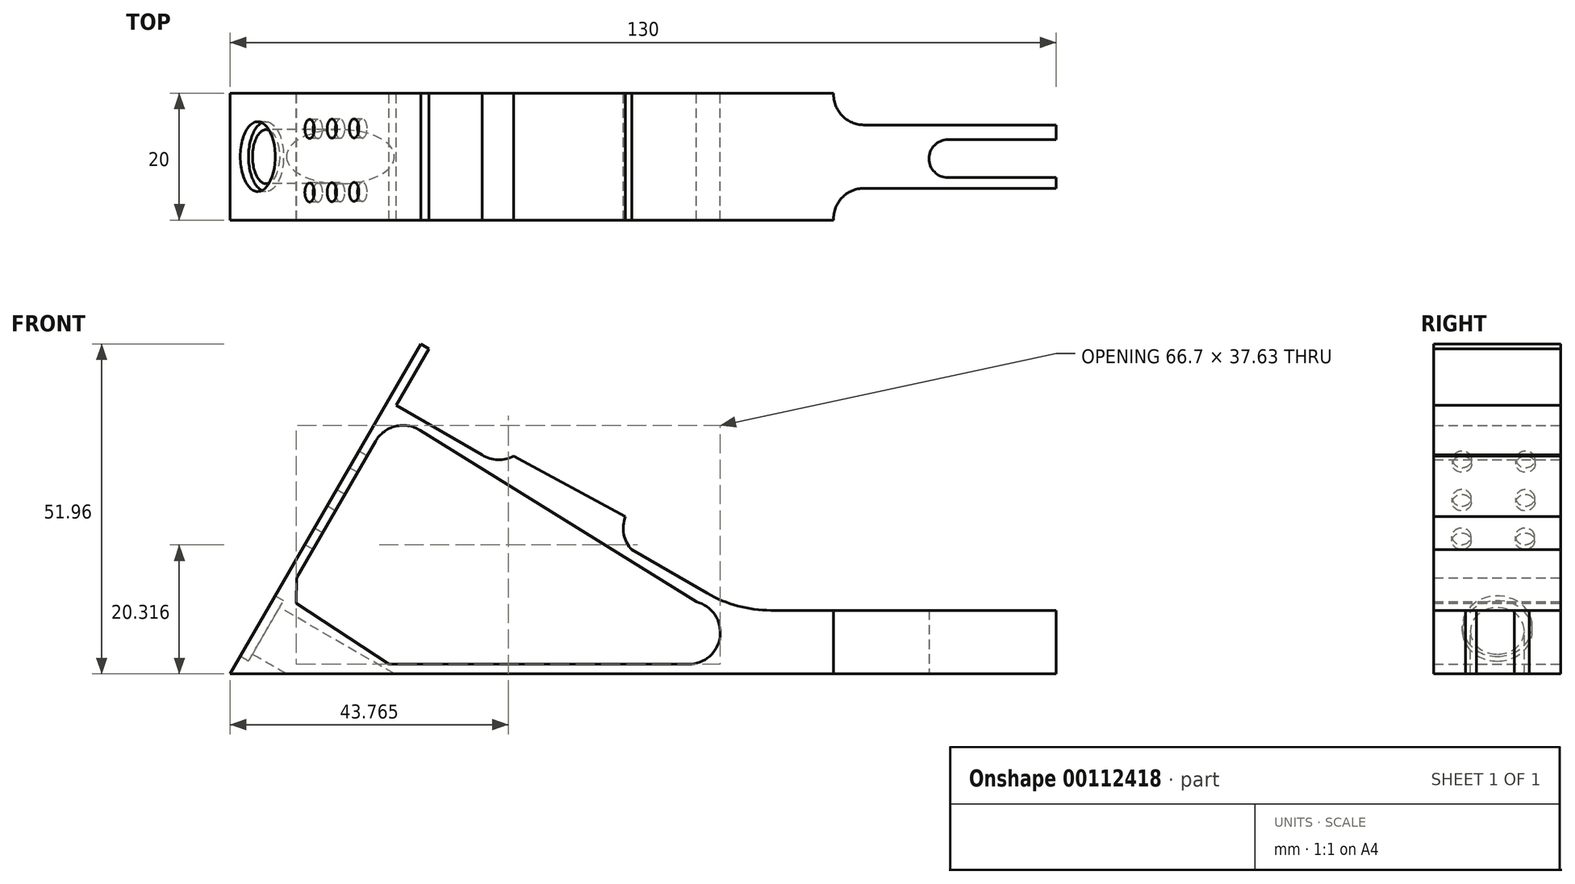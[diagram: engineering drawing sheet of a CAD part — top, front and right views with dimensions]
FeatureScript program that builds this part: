
annotation { "Feature Type Name" : "Feature", "Feature Type Description" : "" }
export const myFeature = defineFeature(function(context is Context, id is Id, definition is map)
    precondition{}
    {
        {
            var Q0;
            Q0=qCreatedBy(makeId("Front.planeOp"),FACE);
            var sketch = newSketch(context, id + "F0", { "sketchPlane" : qUnion([Q0])});
            skLineSegment(sketch, "E0", {"start": v(0, 0) * mm, "end": v(130, 0) * mm});
            skLineSegment(sketch, "E1", {"start": v(30, 51.96) * mm, "end": v(0, 0) * mm});
            skLineSegment(sketch, "E2", {"start": v(130, 0) * mm, "end": v(130, 10) * mm});
            skLineSegment(sketch, "E3", {"start": v(130, 10) * mm, "end": v(85.1, 10) * mm});
            skLineSegment(sketch, "E4", {"start": v(75.1, 12.68) * mm, "end": v(63.23, 19.53) * mm});
            skLineSegment(sketch, "E5", {"start": v(62.2, 24.74) * mm, "end": v(44.64, 34.31) * mm});
            skLineSegment(sketch, "E6", {"start": v(39.66, 34.46) * mm, "end": v(26.13, 42.26) * mm});
            skLineSegment(sketch, "E7", {"start": v(26.13, 42.26) * mm, "end": v(31.3, 51.21) * mm});
            skLineSegment(sketch, "E8", {"start": v(31.3, 51.21) * mm, "end": v(30, 51.96) * mm});
            skArc(sketch, "E9.filletArc", {"start": v(75.1, 12.68) * mm, "mid": v(79.93, 10.68) * mm, "end": v(85.1, 10) * mm});
            skArc(sketch, "E10", {"start": v(44.64, 34.31) * mm, "mid": v(42.13, 33.72) * mm, "end": v(39.66, 34.46) * mm});
            skArc(sketch, "E11", {"start": v(62.2, 24.74) * mm, "mid": v(61.97, 22) * mm, "end": v(63.23, 19.53) * mm});
            skLineSegment(sketch, "E12", {"start": v(10.46, 15.12) * mm, "end": v(22.88, 36.64) * mm});
            skLineSegment(sketch, "E13", {"start": v(29.85, 38.39) * mm, "end": v(73.39, 11.35) * mm});
            skPoint(sketch, "E14.visualSharp", {"position": v(25.47, 41.1) * mm});
            skArc(sketch, "E14.filletArc", {"start": v(29.85, 38.39) * mm, "mid": v(26, 38.99) * mm, "end": v(22.88, 36.64) * mm});
            skLineSegment(sketch, "E15", {"start": v(10.46, 15.12) * mm, "end": v(10.42, 11.1) * mm});
            skLineSegment(sketch, "E16", {"start": v(10.42, 11.1) * mm, "end": v(25, 1.5) * mm});
            skLineSegment(sketch, "E17", {"start": v(25, 1.5) * mm, "end": v(72.15, 1.5) * mm});
            skArc(sketch, "E18", {"start": v(72.15, 1.5) * mm, "mid": v(77.11, 5.88) * mm, "end": v(73.39, 11.35) * mm});
            skSolve(sketch);
        }
        {
            var Q0;
            Q0 = qSketchRegion(id + "F0", true);
            extrude(context, id + "F1", {"entities" : qUnion([Q0]), "depth" : 20 * mm});
        }
        {
            var Q0;
            Q0=makeQuery(id+"F1.opExtrude","SWEPT_EDGE",EDGE,{"disambiguationData":[OSD([sQuery(id+"F0.wireOp",EDGE,"E2"),sQuery(id+"F0.wireOp",EDGE,"E3")])]});
            cPlane(context, id + "F2", {"entities" : qUnion([Q0]), "cplaneType" : CPlaneType.LINE_ANGLE, "offset" : 25 * mm, "angle" : 45 * degree, "width" : 150 * mm, "height" : 150 * mm});
        }
        {
            var Q0;
            Q0=qCreatedBy(id+"F2.planeOp",FACE);
            var sketch = newSketch(context, id + "F3", { "sketchPlane" : qUnion([Q0])});
            skLineSegment(sketch, "E19", {"start": v(13.04, -9.66) * mm, "end": v(21.04, -9.66) * mm});
            skArc(sketch, "E20.0.startCap", {"start": v(13.04, -13.66) * mm, "mid": v(9.04, -9.66) * mm, "end": v(13.04, -5.66) * mm});
            skArc(sketch, "E20.0.endCap", {"start": v(21.04, -5.66) * mm, "mid": v(25.04, -9.66) * mm, "end": v(21.04, -13.66) * mm});
            skLineSegment(sketch, "E20.0.left", {"start": v(13.04, -5.66) * mm, "end": v(21.04, -5.66) * mm});
            skLineSegment(sketch, "E20.0.right", {"start": v(13.04, -13.66) * mm, "end": v(21.04, -13.66) * mm});
            skSolve(sketch);
        }
        {
            var Q0;
            Q0 = qSketchRegion(id + "F3", true);
            extrude(context, id + "F4", {"entities" : qUnion([Q0]), "operationType" : NewBodyOperationType.REMOVE, "oppositeDirection" : true, "depth" : 50 * mm});
        }
        {
            var Q0;
            Q0=qCreatedBy(makeId("Top.planeOp"),FACE);
            var sketch = newSketch(context, id + "F5", { "sketchPlane" : qUnion([Q0])});
            skLineSegment(sketch, "E21", {"start": v(95, 0) * mm, "end": v(130, 0) * mm});
            skLineSegment(sketch, "E22", {"start": v(95, -20) * mm, "end": v(130, -20) * mm});
            skLineSegment(sketch, "E23", {"start": v(130, -20) * mm, "end": v(130, -15) * mm});
            skLineSegment(sketch, "E24", {"start": v(130, -5) * mm, "end": v(99.74, -5) * mm});
            skLineSegment(sketch, "E25", {"start": v(130, -15) * mm, "end": v(99.74, -15) * mm});
            skLineSegment(sketch, "E26", {"start": v(130, -13.3) * mm, "end": v(113, -13.3) * mm});
            skLineSegment(sketch, "E27", {"start": v(130, -7.3) * mm, "end": v(113, -7.3) * mm});
            skArc(sketch, "E28", {"start": v(113, -7.3) * mm, "mid": v(110, -10.3) * mm, "end": v(113, -13.3) * mm});
            skLineSegment(sketch, "E29", {"start": v(113, -13.3) * mm, "end": v(113, -7.3) * mm});
            skLineSegment(sketch, "E30", {"start": v(130, 0) * mm, "end": v(130, -5) * mm});
            skArc(sketch, "E31", {"start": v(99.74, -15) * mm, "mid": v(96.3, -16.48) * mm, "end": v(95, -20) * mm});
            skArc(sketch, "E32", {"start": v(99.74, -5) * mm, "mid": v(96.3, -3.52) * mm, "end": v(95, 0) * mm});
            skLineSegment(sketch, "E33.trimOffspring", {"start": v(130, -13.3) * mm, "end": v(130, -7.3) * mm});
            skLineSegment(sketch, "E34.trimOffspring", {"start": v(130, -5) * mm, "end": v(130, 0) * mm});
            skSolve(sketch);
        }
        {
            var Q0;
            Q0 = qSketchRegion(id + "F5", true);
            extrude(context, id + "F6", {"entities" : qUnion([Q0]), "operationType" : NewBodyOperationType.REMOVE, "depth" : 25 * mm});
        }
        {
            var Q0;
            Q0=makeQuery(id+"F1.opExtrude","SWEPT_EDGE",EDGE,{"disambiguationData":[OSD([sQuery(id+"F0.wireOp",EDGE,"E0"),sQuery(id+"F0.wireOp",EDGE,"E1")])]});
            cPlane(context, id + "F7", {"entities" : qUnion([Q0]), "cplaneType" : CPlaneType.LINE_ANGLE, "offset" : 25 * mm, "angle" : 120 * degree, "width" : 150 * mm, "height" : 150 * mm});
        }
        {
            var Q0;
            Q0=qCreatedBy(id+"F7.planeOp",FACE);
            var sketch = newSketch(context, id + "F8", { "sketchPlane" : qUnion([Q0])});
            skCircle(sketch, "E35", {"center": v(-10, 8.68) * mm, "radius": 4.25 * mm});
            skCircle(sketch, "E36", {"center": v(-5.64, 25) * mm, "radius": 1.5 * mm});
            skCircle(sketch, "E37", {"center": v(-15.64, 25) * mm, "radius": 1.5 * mm});
            skCircle(sketch, "E38.1.0.0", {"center": v(-5.6, 32) * mm, "radius": 1.5 * mm});
            skCircle(sketch, "E38.2.0.0", {"center": v(-5.55, 39) * mm, "radius": 1.5 * mm});
            skLineSegment(sketch, "E38.direction1", {"start": v(-5.64, 25) * mm, "end": v(-5.6, 32) * mm, "construction": true});
            skCircle(sketch, "E39.1.0.0", {"center": v(-15.6, 32) * mm, "radius": 1.5 * mm});
            skCircle(sketch, "E39.2.0.0", {"center": v(-15.55, 39) * mm, "radius": 1.5 * mm});
            skLineSegment(sketch, "E39.direction1", {"start": v(-15.64, 25) * mm, "end": v(-15.6, 32) * mm, "construction": true});
            skSolve(sketch);
        }
        {
            var Q0;
            Q0 = qSketchRegion(id + "F8", true);
            extrude(context, id + "F9", {"entities" : qUnion([Q0]), "operationType" : NewBodyOperationType.REMOVE, "depth" : 25 * mm});
        }
        {
            var Q0;
            Q0=qCreatedBy(id+"F7.planeOp",FACE);
            var sketch = newSketch(context, id + "F10", { "sketchPlane" : qUnion([Q0])});
            skCircle(sketch, "E40", {"center": v(-10, 8.68) * mm, "radius": 5.5 * mm});
            skSolve(sketch);
        }
        {
            var Q0;
            Q0 = qSketchRegion(id + "F10", true);
            extrude(context, id + "F11", {"entities" : qUnion([Q0]), "operationType" : NewBodyOperationType.REMOVE, "depth" : 1.5 * mm});
        }
    });
